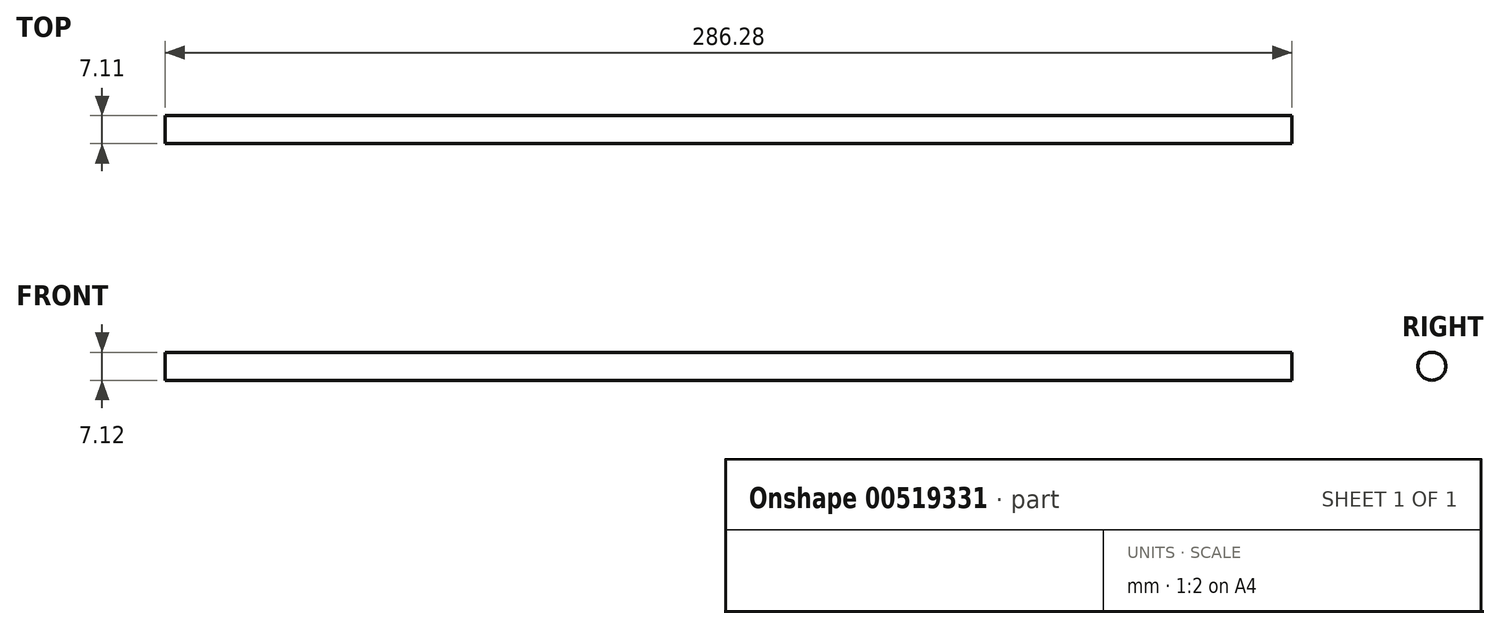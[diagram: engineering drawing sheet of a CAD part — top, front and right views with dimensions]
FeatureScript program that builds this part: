
annotation { "Feature Type Name" : "Feature", "Feature Type Description" : "" }
export const myFeature = defineFeature(function(context is Context, id is Id, definition is map)
    precondition{}
    {
        {
            var Q0;
            Q0=qCreatedBy(makeId("Top.planeOp"),FACE);
            var sketch = newSketch(context, id + "F0", { "sketchPlane" : qUnion([Q0])});
            skLineSegment(sketch, "E0.bottom", {"start": v(-139.4, 0) * mm, "end": v(146.9, 0) * mm});
            skLineSegment(sketch, "E0.top", {"start": v(-139.4, -3.56) * mm, "end": v(146.9, -3.56) * mm});
            skLineSegment(sketch, "E0.left", {"start": v(-139.4, 0) * mm, "end": v(-139.4, -3.56) * mm});
            skLineSegment(sketch, "E0.right", {"start": v(146.9, 0) * mm, "end": v(146.9, -3.56) * mm});
            skSolve(sketch);
        }
        {
            var Q0;
            Q0=makeQuery(id+"F0.imprint","IMPRINT",FACE,{"disambiguationData":[TD([[makeQuery(id+"F0.imprint","IMPRINT",EDGE,{"derivedFrom":sQuery(id+"F0.wireOp",EDGE,"E0.bottom")}),-1.0]])]});
            var Q1;
            Q1=sQuery(id+"F0.wireOp",EDGE,"E0.top");
            revolve(context, id + "F1", {"entities" : qUnion([Q0]), "axis" : qUnion([Q1]), "revolveType" : RevolveType.FULL});
        }
    });
